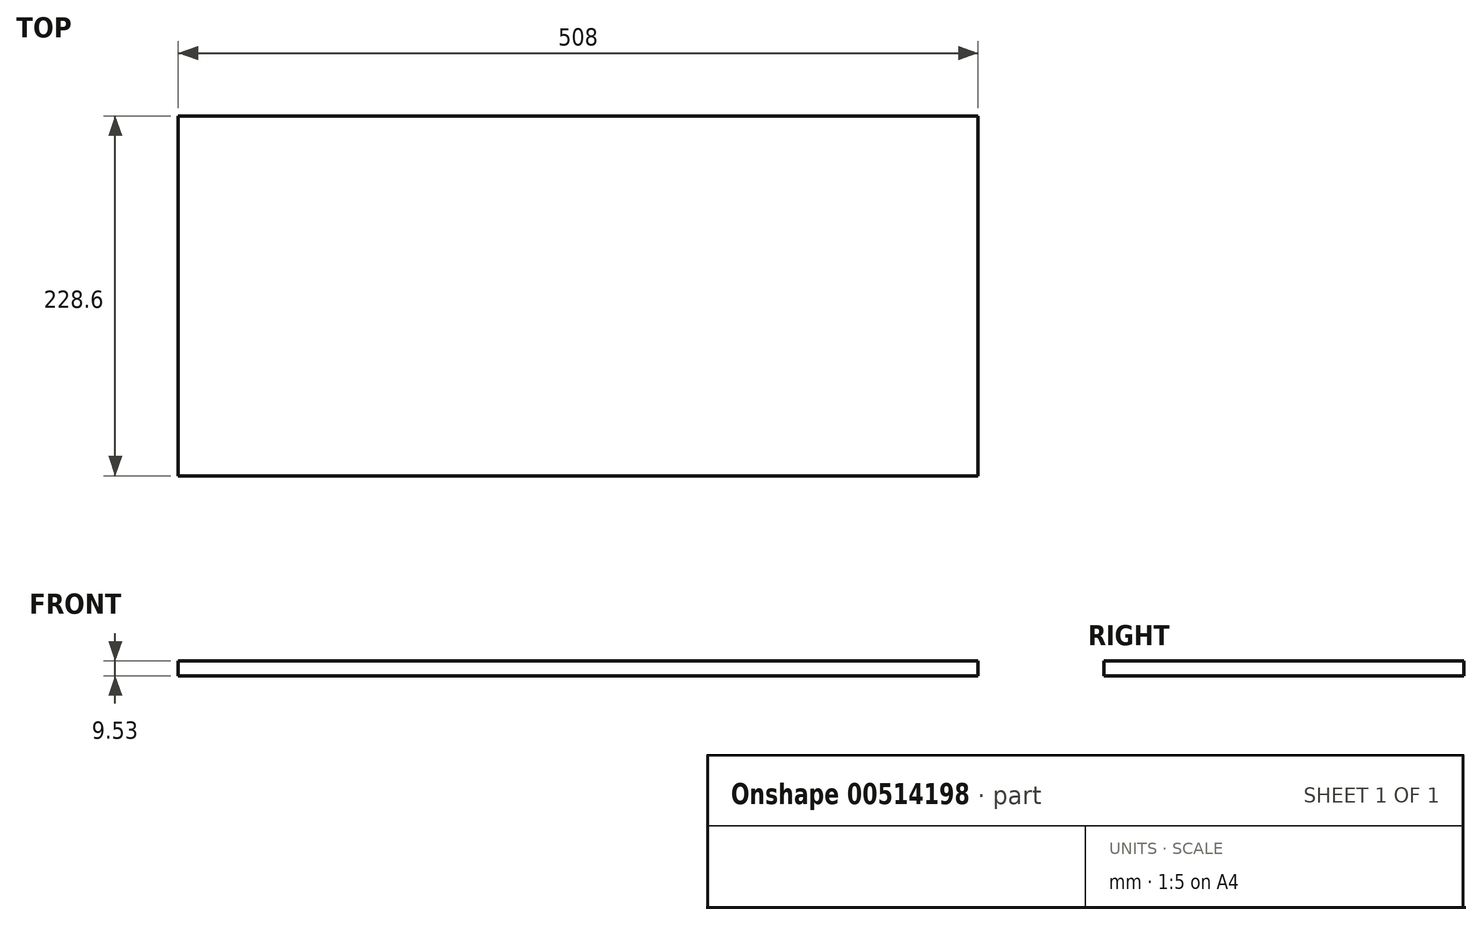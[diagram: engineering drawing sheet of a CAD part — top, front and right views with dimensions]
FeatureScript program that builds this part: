
annotation { "Feature Type Name" : "Feature", "Feature Type Description" : "" }
export const myFeature = defineFeature(function(context is Context, id is Id, definition is map)
    precondition{}
    {
        {
            var Q0;
            Q0=qCreatedBy(makeId("Top.planeOp"),FACE);
            var sketch = newSketch(context, id + "F0", { "sketchPlane" : qUnion([Q0]), "disableImprinting" : false});
            skLineSegment(sketch, "E0.bottom", {"start": v(-249.38, 59.27) * mm, "end": v(258.62, 59.27) * mm});
            skLineSegment(sketch, "E0.top", {"start": v(-249.38, -169.33) * mm, "end": v(258.62, -169.33) * mm});
            skLineSegment(sketch, "E0.left", {"start": v(-249.38, 59.27) * mm, "end": v(-249.38, -169.33) * mm});
            skLineSegment(sketch, "E0.right", {"start": v(258.62, 59.27) * mm, "end": v(258.62, -169.33) * mm});
            skSolve(sketch);
        }
        {
            var Q0;
            Q0 = qSketchRegion(id + "F0", true);
            extrude(context, id + "F1", {"entities" : qUnion([Q0]), "flatOperationType" : FlatOperationType.REMOVE, "depth" : 9.52 * mm, "offsetDistance" : 25.4 * mm, "domain" : OperationDomain.MODEL});
        }
    });
